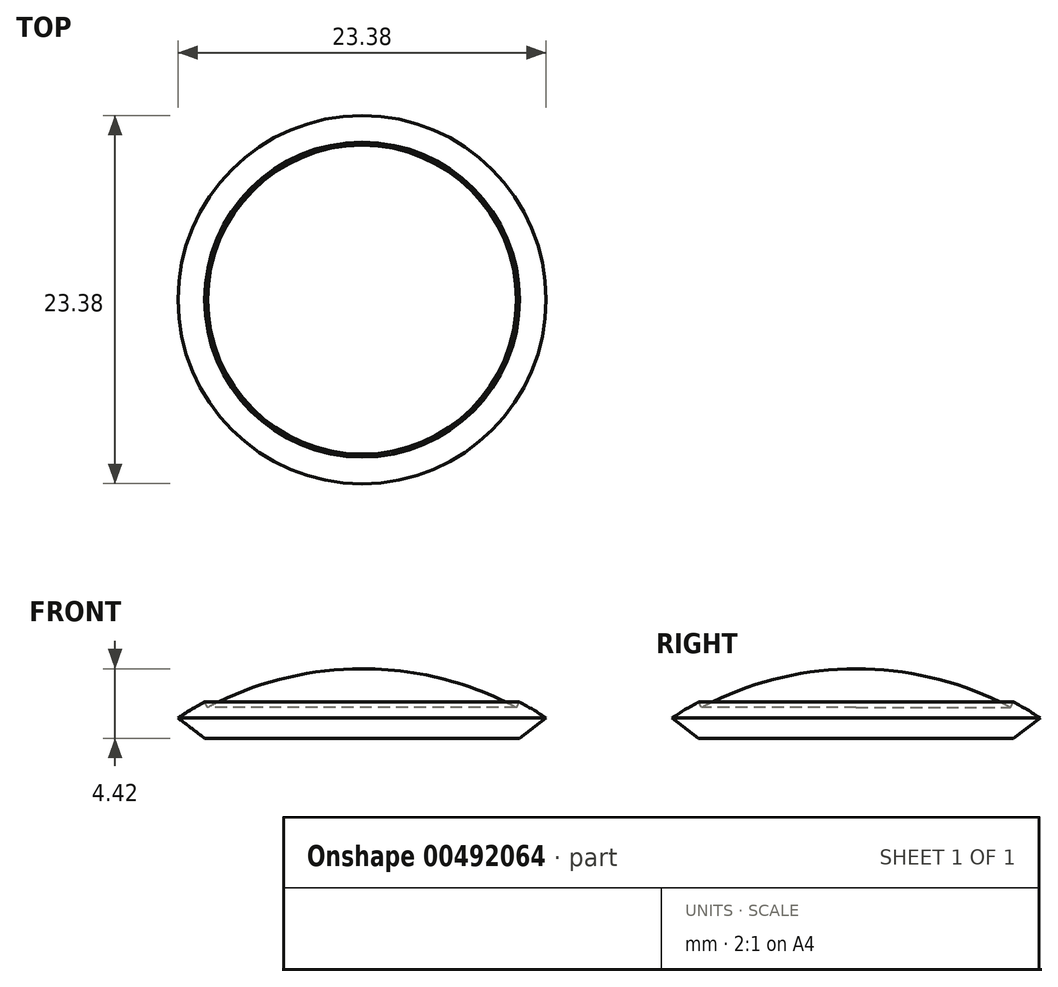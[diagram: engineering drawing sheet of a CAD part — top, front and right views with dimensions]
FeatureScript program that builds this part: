
annotation { "Feature Type Name" : "Feature", "Feature Type Description" : "" }
export const myFeature = defineFeature(function(context is Context, id is Id, definition is map)
    precondition{}
    {
        {
            var Q0;
            Q0=qCreatedBy(makeId("Front.planeOp"),FACE);
            var sketch = newSketch(context, id + "F0", { "sketchPlane" : qUnion([Q0])});
            skArc(sketch, "E0", {"start": v(10, 0) * mm, "mid": v(0, 2.82) * mm, "end": v(-10, 0) * mm});
            skLineSegment(sketch, "E1", {"start": v(0, -16.35) * mm, "end": v(0, 0) * mm, "construction": true});
            skArc(sketch, "E2.0", {"start": v(11.33, 1.05) * mm, "mid": v(0, 4.42) * mm, "end": v(-11.33, 1.05) * mm});
            skArc(sketch, "E3.0", {"start": v(11.7, 1.3) * mm, "mid": v(10.86, 1.82) * mm, "end": v(10, 2.3) * mm});
            skLineSegment(sketch, "E4", {"start": v(-11.7, 1.3) * mm, "end": v(-10, 0) * mm});
            skLineSegment(sketch, "E5", {"start": v(11.7, 1.3) * mm, "end": v(10, 0) * mm});
            skLineSegment(sketch, "E6", {"start": v(-10, 2.3) * mm, "end": v(-9.06, 0.54) * mm});
            skLineSegment(sketch, "E7", {"start": v(9.06, 0.54) * mm, "end": v(10, 2.3) * mm});
            skArc(sketch, "E8.trimOffspring", {"start": v(-10, 2.3) * mm, "mid": v(-10.86, 1.82) * mm, "end": v(-11.7, 1.3) * mm});
            skLineSegment(sketch, "E9", {"start": v(0, 0) * mm, "end": v(0, 4.42) * mm});
            skLineSegment(sketch, "E10", {"start": v(0, 0) * mm, "end": v(-10, 0) * mm});
            skSolve(sketch);
        }
        {
            var Q0;
            {var subQ0=sQuery(id+"F0.wireOp",EDGE,"E6");var subQ1=sQuery(id+"F0.wireOp",EDGE,"E0");var subQ2=makeQuery(id+"F0.imprint","INTERSECT",VERTEX,{"derivedFrom":[subQ1,subQ0]});Q0=makeQuery(id+"F0.imprint","IMPRINT",FACE,{"disambiguationData":[TD([[makeQuery(id+"F0.imprint","IMPRINT",EDGE,{"disambiguationData":[TD([[subQ2,1.0]])],"derivedFrom":subQ1}),-1.0]])]});}
            var Q1;
            {var subQ5=sQuery(id+"F0.wireOp",EDGE,"E4");Q1=makeQuery(id+"F0.imprint","IMPRINT",FACE,{"disambiguationData":[TD([[makeQuery(id+"F0.imprint","IMPRINT",EDGE,{"derivedFrom":subQ5}),1.0]])]});}
            var Q2;
            {var subQ4=sQuery(id+"F0.wireOp",EDGE,"E10");Q2=makeQuery(id+"F0.imprint","IMPRINT",FACE,{"disambiguationData":[TD([[makeQuery(id+"F0.imprint","IMPRINT",EDGE,{"derivedFrom":subQ4}),-1.0]])]});}
            var Q3;
            Q3=sQuery(id+"F0.wireOp",EDGE,"E9");
            revolve(context, id + "F1", {"entities" : qUnion([Q0, Q1, Q2]), "axis" : qUnion([Q3]), "revolveType" : RevolveType.FULL});
        }
    });
